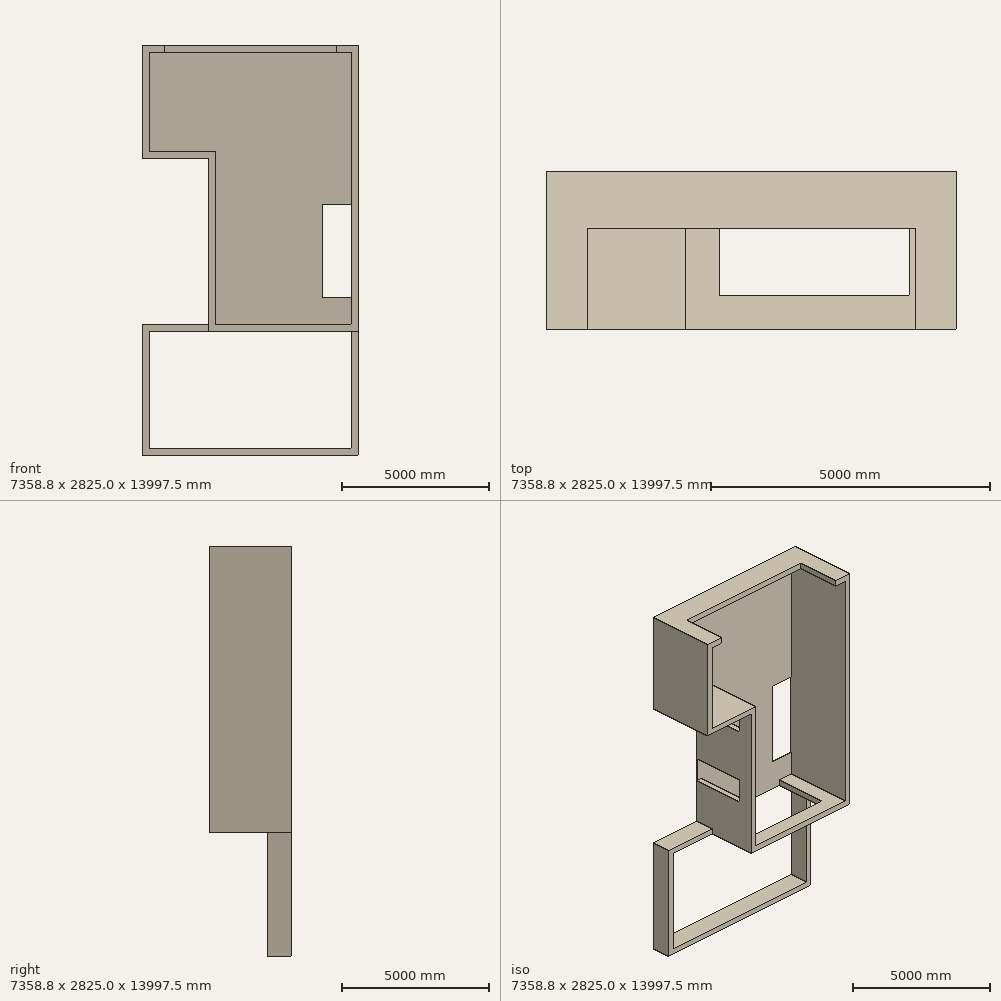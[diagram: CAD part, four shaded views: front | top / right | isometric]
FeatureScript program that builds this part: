
annotation { "Feature Type Name" : "Feature", "Feature Type Description" : "" }
export const myFeature = defineFeature(function(context is Context, id is Id, definition is map)
    precondition{}
    {
        {
            var Q0;
            Q0=qCreatedBy(makeId("Front.planeOp"),FACE);
            var sketch = newSketch(context, id + "F0", { "sketchPlane" : qUnion([Q0])});
            skLineSegment(sketch, "E0", {"start": v(0, 0) * mm, "end": v(6900, 0) * mm});
            skLineSegment(sketch, "E1", {"start": v(0, 0) * mm, "end": v(0, -3400) * mm});
            skLineSegment(sketch, "E2", {"start": v(0, -3400) * mm, "end": v(2260, -3400) * mm});
            skLineSegment(sketch, "E3", {"start": v(2260, -3400) * mm, "end": v(2260, -9290) * mm});
            skLineSegment(sketch, "E4", {"start": v(6900, 0) * mm, "end": v(6900, -9290) * mm});
            skLineSegment(sketch, "E5", {"start": v(6900, -9290) * mm, "end": v(2260, -9290) * mm});
            skLineSegment(sketch, "E6.0", {"start": v(-228.6, 228.6) * mm, "end": v(7128.6, 228.6) * mm});
            skLineSegment(sketch, "E6.1", {"start": v(7128.6, -9518.6) * mm, "end": v(2031.4, -9518.6) * mm});
            skLineSegment(sketch, "E6.2", {"start": v(2031.4, -3628.6) * mm, "end": v(2031.4, -9518.6) * mm});
            skLineSegment(sketch, "E6.3", {"start": v(7128.6, 228.6) * mm, "end": v(7128.6, -9518.6) * mm});
            skLineSegment(sketch, "E6.4", {"start": v(-228.6, -3628.6) * mm, "end": v(2031.4, -3628.6) * mm});
            skLineSegment(sketch, "E6.5", {"start": v(-228.6, 228.6) * mm, "end": v(-228.6, -3628.6) * mm});
            skLineSegment(sketch, "E7", {"start": v(6900, -8390) * mm, "end": v(5900, -8390) * mm});
            skLineSegment(sketch, "E8", {"start": v(5900, -8390) * mm, "end": v(5900, -5190) * mm});
            skLineSegment(sketch, "E9", {"start": v(5900, -5190) * mm, "end": v(6900, -5190) * mm});
            skLineSegment(sketch, "E10", {"start": v(6900, -5190) * mm, "end": v(6900, -8390) * mm});
            skLineSegment(sketch, "E11.bottom", {"start": v(5008.33, -11844.36) * mm, "end": v(8061.42, -11844.36) * mm});
            skLineSegment(sketch, "E11.top", {"start": v(5008.33, -17402.37) * mm, "end": v(8061.42, -17402.37) * mm});
            skLineSegment(sketch, "E11.left", {"start": v(5008.33, -11844.36) * mm, "end": v(5008.33, -17402.37) * mm});
            skLineSegment(sketch, "E11.right", {"start": v(8061.42, -11844.36) * mm, "end": v(8061.42, -17402.37) * mm});
            skLineSegment(sketch, "E12.bottom", {"start": v(5749.13, -12613) * mm, "end": v(7348.5, -12613) * mm});
            skLineSegment(sketch, "E12.top", {"start": v(5749.13, -16807.53) * mm, "end": v(7348.5, -16807.53) * mm});
            skLineSegment(sketch, "E12.left", {"start": v(5749.13, -12613) * mm, "end": v(5749.13, -16807.53) * mm});
            skLineSegment(sketch, "E12.right", {"start": v(7348.5, -12613) * mm, "end": v(7348.5, -16807.53) * mm});
            skSolve(sketch);
        }
        {
            var Q0;
            Q0=makeQuery(id+"F0.imprint","IMPRINT",FACE,{"disambiguationData":[TD([[makeQuery(id+"F0.imprint","IMPRINT",EDGE,{"derivedFrom":sQuery(id+"F0.wireOp",EDGE,"E0")}),1.0]])]});
            extrude(context, id + "F1", {"entities" : qUnion([Q0]), "depth" : 2800 * mm});
        }
        {
            var Q0;
            Q0=makeQuery(id+"F1.opExtrude","SWEPT_FACE",FACE,{"disambiguationData":[OSD([sQuery(id+"F0.wireOp",EDGE,"E0")])]});
            var sketch = newSketch(context, id + "F2", { "sketchPlane" : qUnion([Q0])});
            skLineSegment(sketch, "E13", {"start": v(0, 0) * mm, "end": v(0, 1000) * mm});
            skLineSegment(sketch, "E14", {"start": v(6900, 1000) * mm, "end": v(6900, 2800) * mm});
            skLineSegment(sketch, "E15", {"start": v(0, 2800) * mm, "end": v(0, 1000) * mm});
            skLineSegment(sketch, "E16", {"start": v(0, 1000) * mm, "end": v(500, 1000) * mm});
            skLineSegment(sketch, "E17", {"start": v(500, 1000) * mm, "end": v(500, 2800) * mm});
            skLineSegment(sketch, "E18", {"start": v(500, 2800) * mm, "end": v(6400, 2800) * mm});
            skLineSegment(sketch, "E19", {"start": v(6400, 2800) * mm, "end": v(6400, 1000) * mm});
            skLineSegment(sketch, "E20", {"start": v(6400, 1000) * mm, "end": v(6900, 1000) * mm});
            skLineSegment(sketch, "E21", {"start": v(500, 1000) * mm, "end": v(6400, 1000) * mm});
            skSolve(sketch);
        }
        {
            var Q0;
            Q0=makeQuery(id+"F2.imprint","IMPRINT",FACE,{"disambiguationData":[TD([[makeQuery(id+"F2.imprint","IMPRINT",EDGE,{"derivedFrom":sQuery(id+"F2.wireOp",EDGE,"E17")}),-1.0]])]});
            extrude(context, id + "F3", {"entities" : qUnion([Q0]), "operationType" : NewBodyOperationType.REMOVE, "oppositeDirection" : true, "depth" : 1040 * mm});
        }
        {
            var Q0;
            Q0=makeQuery(id+"F1.opExtrude","SWEPT_FACE",FACE,{"disambiguationData":[OSD([sQuery(id+"F0.wireOp",EDGE,"E6.1")])]});
            var sketch = newSketch(context, id + "F4", { "sketchPlane" : qUnion([Q0])});
            skLineSegment(sketch, "E22", {"start": v(7128.6, 0) * mm, "end": v(6278.6, 0) * mm});
            skLineSegment(sketch, "E23", {"start": v(6278.6, 0) * mm, "end": v(6278.6, 2200) * mm});
            skLineSegment(sketch, "E24", {"start": v(6278.6, 2200) * mm, "end": v(2878.6, 2200) * mm});
            skLineSegment(sketch, "E25", {"start": v(2878.6, 2200) * mm, "end": v(2878.6, 0) * mm});
            skLineSegment(sketch, "E26", {"start": v(2878.6, 0) * mm, "end": v(6278.6, 0) * mm});
            skSolve(sketch);
        }
        {
            var Q0;
            Q0=makeQuery(id+"F4.imprint","IMPRINT",FACE,{"disambiguationData":[TD([[makeQuery(id+"F4.imprint","IMPRINT",EDGE,{"derivedFrom":sQuery(id+"F4.wireOp",EDGE,"E23")}),1.0]])]});
            extrude(context, id + "F5", {"entities" : qUnion([Q0]), "operationType" : NewBodyOperationType.REMOVE, "oppositeDirection" : true, "depth" : 530.02 * mm});
        }
        {
            var Q0;
            Q0=makeQuery(id+"F1.opExtrude","CAP_FACE",FACE,{"disambiguationData":[OSD([sQuery(id+"F0.wireOp",EDGE,"E0"),sQuery(id+"F0.wireOp",EDGE,"E1"),sQuery(id+"F0.wireOp",EDGE,"E2"),sQuery(id+"F0.wireOp",EDGE,"E3"),sQuery(id+"F0.wireOp",EDGE,"E4"),sQuery(id+"F0.wireOp",EDGE,"E5"),sQuery(id+"F0.wireOp",EDGE,"E6.0"),sQuery(id+"F0.wireOp",EDGE,"E6.1"),sQuery(id+"F0.wireOp",EDGE,"E6.2"),sQuery(id+"F0.wireOp",EDGE,"E6.3"),sQuery(id+"F0.wireOp",EDGE,"E6.4"),sQuery(id+"F0.wireOp",EDGE,"E6.5")])],"isStart":true});
            var sketch = newSketch(context, id + "F6", { "sketchPlane" : qUnion([Q0])});
            skLineSegment(sketch, "E27", {"start": v(228.6, 228.6) * mm, "end": v(-7128.6, 228.6) * mm});
            skLineSegment(sketch, "E28", {"start": v(-7128.6, 228.6) * mm, "end": v(-7128.6, -9518.6) * mm});
            skLineSegment(sketch, "E29", {"start": v(-7128.6, -9518.6) * mm, "end": v(-2031.4, -9518.6) * mm});
            skLineSegment(sketch, "E30", {"start": v(-2031.4, -9518.6) * mm, "end": v(-2031.4, -3628.6) * mm});
            skLineSegment(sketch, "E31", {"start": v(-2031.4, -3628.6) * mm, "end": v(228.6, -3628.6) * mm});
            skLineSegment(sketch, "E32", {"start": v(228.6, -3628.6) * mm, "end": v(228.6, 228.6) * mm});
            skLineSegment(sketch, "E33", {"start": v(-6900, -9290) * mm, "end": v(-6900, -8390) * mm});
            skLineSegment(sketch, "E34", {"start": v(-6900, -8390) * mm, "end": v(-5900, -8390) * mm});
            skLineSegment(sketch, "E35", {"start": v(-5900, -8390) * mm, "end": v(-5900, -5190) * mm});
            skLineSegment(sketch, "E36", {"start": v(-5900, -5190) * mm, "end": v(-6900, -5190) * mm});
            skLineSegment(sketch, "E37", {"start": v(-6900, -5190) * mm, "end": v(-6900, -8390) * mm});
            skSolve(sketch);
        }
        {
            var Q0;
            Q0 = qSketchRegion(id + "F6", true);
            extrude(context, id + "F7", {"entities" : qUnion([Q0]), "operationType" : NewBodyOperationType.ADD, "depth" : 25 * mm});
        }
        {
            var Q0;
            Q0=makeQuery(id+"F1.opExtrude","SWEPT_FACE",FACE,{"disambiguationData":[OSD([sQuery(id+"F0.wireOp",EDGE,"E3")])]});
            var sketch = newSketch(context, id + "F8", { "sketchPlane" : qUnion([Q0])});
            skLineSegment(sketch, "E38", {"start": v(0, -3400) * mm, "end": v(0, -3704.8) * mm});
            skLineSegment(sketch, "E39", {"start": v(0, -3704.8) * mm, "end": v(-2200, -3704.8) * mm});
            skLineSegment(sketch, "E40", {"start": v(-2200, -3704.8) * mm, "end": v(-2200, -4624.8) * mm});
            skLineSegment(sketch, "E41", {"start": v(-2200, -4624.8) * mm, "end": v(0, -4624.8) * mm});
            skLineSegment(sketch, "E42", {"start": v(0, -4624.8) * mm, "end": v(0, -6664.8) * mm});
            skLineSegment(sketch, "E43", {"start": v(0, -6664.8) * mm, "end": v(-2200, -6664.8) * mm});
            skLineSegment(sketch, "E44", {"start": v(-2200, -6664.8) * mm, "end": v(-2200, -7584.8) * mm});
            skLineSegment(sketch, "E45", {"start": v(-2200, -7584.8) * mm, "end": v(0, -7584.8) * mm});
            skSolve(sketch);
        }
        {
            var Q0;
            {var subQ0=sQuery(id+"F8.wireOp",EDGE,"E43");Q0=makeQuery(id+"F8.imprint","IMPRINT",FACE,{"disambiguationData":[TD([[makeQuery(id+"F8.imprint","IMPRINT",EDGE,{"derivedFrom":subQ0}),1.0]])]});}
            var Q1;
            {var subQ0=sQuery(id+"F8.wireOp",EDGE,"E39");Q1=makeQuery(id+"F8.imprint","IMPRINT",FACE,{"disambiguationData":[TD([[makeQuery(id+"F8.imprint","IMPRINT",EDGE,{"derivedFrom":subQ0}),1.0]])]});}
            extrude(context, id + "F9", {"entities" : qUnion([Q0, Q1]), "operationType" : NewBodyOperationType.REMOVE, "oppositeDirection" : true, "depth" : 1000 * mm});
        }
        {
            var Q0;
            Q0=qCreatedBy(makeId("Front.planeOp"),FACE);
            var sketch = newSketch(context, id + "F10", { "sketchPlane" : qUnion([Q0])});
            skLineSegment(sketch, "E46", {"start": v(7127.78, -9518.85) * mm, "end": v(7127.78, -13768.85) * mm});
            skLineSegment(sketch, "E47", {"start": v(7127.78, -13768.85) * mm, "end": v(-230.22, -13768.85) * mm});
            skLineSegment(sketch, "E48", {"start": v(-1.22, -13539.85) * mm, "end": v(6898.78, -13539.85) * mm});
            skLineSegment(sketch, "E49", {"start": v(6898.78, -13539.85) * mm, "end": v(6898.78, -9518.85) * mm});
            skLineSegment(sketch, "E50", {"start": v(6898.78, -9518.85) * mm, "end": v(7127.78, -9518.85) * mm});
            skLineSegment(sketch, "E51", {"start": v(-1.22, -13539.85) * mm, "end": v(-1.22, -9518.85) * mm});
            skLineSegment(sketch, "E52", {"start": v(-230.22, -13768.85) * mm, "end": v(-230.22, -9289.85) * mm});
            skLineSegment(sketch, "E53", {"start": v(-230.22, -9289.85) * mm, "end": v(2018.46, -9289.85) * mm});
            skLineSegment(sketch, "E54", {"start": v(2018.46, -9289.85) * mm, "end": v(2018.46, -9518.85) * mm});
            skLineSegment(sketch, "E55", {"start": v(2018.46, -9518.85) * mm, "end": v(-1.22, -9518.85) * mm});
            skSolve(sketch);
        }
        {
            var Q0;
            Q0=makeQuery(id+"F10.imprint","IMPRINT",FACE,{"disambiguationData":[TD([[makeQuery(id+"F10.imprint","IMPRINT",EDGE,{"derivedFrom":sQuery(id+"F10.wireOp",EDGE,"E46")}),-1.0]])]});
            extrude(context, id + "F11", {"entities" : qUnion([Q0]), "depth" : 790 * mm});
        }
    });
